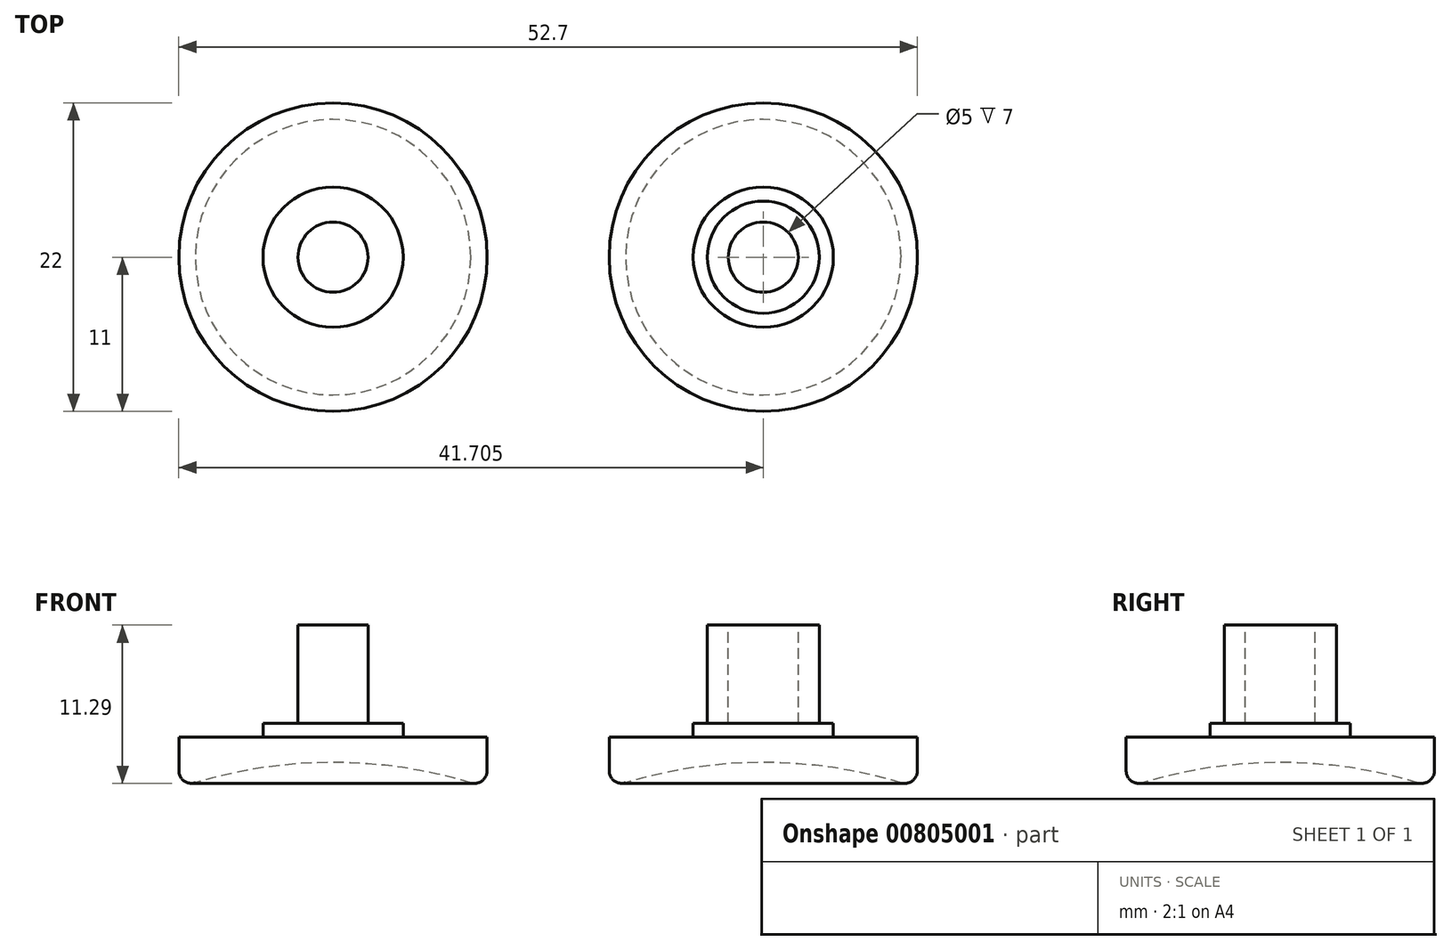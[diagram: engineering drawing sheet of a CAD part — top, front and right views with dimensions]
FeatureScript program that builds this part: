
annotation { "Feature Type Name" : "Feature", "Feature Type Description" : "" }
export const myFeature = defineFeature(function(context is Context, id is Id, definition is map)
    precondition{}
    {
        {
            var Q0;
            Q0=qCreatedBy(makeId("Top.planeOp"),FACE);
            var sketch = newSketch(context, id + "F0", { "sketchPlane" : qUnion([Q0])});
            skCircle(sketch, "E0", {"center": v(59.41, 64.06) * mm, "radius": 11 * mm});
            skSolve(sketch);
        }
        {
            var Q0;
            Q0=makeQuery(id+"F0.imprint","IMPRINT",FACE,{"disambiguationData":[TD([[makeQuery(id+"F0.imprint","IMPRINT",EDGE,{"derivedFrom":sQuery(id+"F0.wireOp",EDGE,"E0")}),1.0]])]});
            var Q1;
            Q1=makeQuery(id+"F0.imprint","IMPRINT",FACE,{"disambiguationData":[TD([[makeQuery(id+"F0.imprint","IMPRINT",EDGE,{"derivedFrom":sQuery(id+"F0.wireOp",EDGE,"2bYrixF8-2V4G-PsJT-iCTY-IxQZrD0WGVvQ")}),1.0]])]});
            extrude(context, id + "F1", {"entities" : qUnion([Q0, Q1]), "depth" : 3.5 * mm, "offsetDistance" : 25 * mm});
        }
        {
            var Q0;
            Q0=makeQuery(id+"F1.opExtrude","CAP_FACE",FACE,{"disambiguationData":[OSD([sQuery(id+"F0.wireOp",EDGE,"E0")])],"isStart":false});
            var sketch = newSketch(context, id + "F2", { "sketchPlane" : qUnion([Q0])});
            skPoint(sketch, "E1", {"position": v(59.41, 64.06) * mm});
            skCircle(sketch, "E2", {"center": v(59.41, 64.06) * mm, "radius": 5 * mm});
            skSolve(sketch);
        }
        {
            var Q0;
            Q0=qSketchRegion(id+"F2",true);
            extrude(context, id + "F3", {"entities" : qUnion([Q0]), "operationType" : NewBodyOperationType.ADD, "depth" : 1 * mm, "offsetDistance" : 25 * mm});
        }
        {
            var Q0;
            Q0=makeQuery(id+"F3.opExtrude","CAP_FACE",FACE,{"disambiguationData":[OSD([sQuery(id+"F2.wireOp",EDGE,"E2")])],"isStart":false});
            var sketch = newSketch(context, id + "F4", { "sketchPlane" : qUnion([Q0])});
            skPoint(sketch, "E3", {"position": v(59.41, 64.06) * mm});
            skCircle(sketch, "E4", {"center": v(59.41, 64.06) * mm, "radius": 4 * mm});
            skSolve(sketch);
        }
        {
            var Q0;
            Q0=makeQuery(id+"F4.imprint","IMPRINT",FACE,{"disambiguationData":[TD([[makeQuery(id+"F4.imprint","IMPRINT",EDGE,{"derivedFrom":sQuery(id+"F4.wireOp",EDGE,"E4")}),1.0]])]});
            extrude(context, id + "F5", {"entities" : qUnion([Q0]), "operationType" : NewBodyOperationType.ADD, "depth" : 7 * mm, "offsetDistance" : 25 * mm});
        }
        {
            var Q0;
            Q0=makeQuery(id+"F1.opExtrude","CAP_FACE",FACE,{"disambiguationData":[OSD([sQuery(id+"F0.wireOp",EDGE,"E0")])],"isStart":true});
            var sketch = newSketch(context, id + "F6", { "sketchPlane" : qUnion([Q0])});
            skCircle(sketch, "E5", {"center": v(59.41, -64.06) * mm, "radius": 1.35 * mm});
            skSolve(sketch);
        }
        {
            var Q0;
            Q0=makeQuery(id+"F6.imprint","IMPRINT",FACE,{"disambiguationData":[TD([[makeQuery(id+"F6.imprint","IMPRINT",EDGE,{"derivedFrom":sQuery(id+"F6.wireOp",EDGE,"E5")}),1.0]])]});
            extrude(context, id + "F7", {"entities" : qUnion([Q0]), "operationType" : NewBodyOperationType.ADD, "depth" : 32.3 * mm, "offsetDistance" : 25 * mm});
        }
        {
            var Q0;
            Q0=makeQuery(id+"F7.opExtrude","CAP_FACE",FACE,{"disambiguationData":[OSD([sQuery(id+"F6.wireOp",EDGE,"E5")])],"isStart":false});
            var sketch = newSketch(context, id + "F8", { "sketchPlane" : qUnion([Q0])});
            skCircle(sketch, "E6", {"center": v(59.41, -64.06) * mm, "radius": 34 * mm});
            skLineSegment(sketch, "E7", {"start": v(59.41, -64.06) * mm, "end": v(93.41, -64.06) * mm});
            skLineSegment(sketch, "E8", {"start": v(59.41, -64.06) * mm, "end": v(25.41, -64.06) * mm});
            skSolve(sketch);
        }
        {
            var Q0;
            {var subQ0=sQuery(id+"F8.wireOp",EDGE,"E7");var subQ1=sQuery(id+"F8.wireOp",EDGE,"E6");var subQ2=makeQuery(id+"F8.imprint","INTERSECT",VERTEX,{"derivedFrom":[subQ1,subQ0]});Q0=makeQuery(id+"F8.imprint","IMPRINT",FACE,{"disambiguationData":[TD([[makeQuery(id+"F8.imprint","IMPRINT",EDGE,{"disambiguationData":[TD([[subQ2,-1.0]])],"derivedFrom":subQ1}),1.0]])]});}
            var Q1;
            {var subQ0=sQuery(id+"F8.wireOp",EDGE,"E8");var subQ1=sQuery(id+"F8.wireOp",EDGE,"E7");var subQ2=makeQuery(id+"F8.imprint","INTERSECT",VERTEX,{"derivedFrom":[subQ1,subQ0]});Q1=makeQuery(id+"F8.imprint","IMPRINT",FACE,{"disambiguationData":[TD([[makeQuery(id+"F8.imprint","IMPRINT",EDGE,{"disambiguationData":[TD([[subQ2,-1.0]])],"derivedFrom":subQ1}),1.0]])]});}
            var Q2;
            Q2=sQuery(id+"F8.wireOp",EDGE,"E7");
            revolve(context, id + "F9", {"operationType" : NewBodyOperationType.REMOVE, "surfaceOperationType" : NewSurfaceOperationType.NEW, "entities" : qUnion([Q0, Q1]), "axis" : qUnion([Q2]), "revolveType" : RevolveType.FULL});
        }
        {
            var Q0;
            Q0=makeQuery(id+"F9.boolean.opBoolean","INTERSECT",EDGE,{"derivedFrom":[makeQuery(id+"F1.opExtrude","CAP_FACE",FACE,{"disambiguationData":[OSD([sQuery(id+"F0.wireOp",EDGE,"E0")])],"isStart":true}),makeQuery(id+"F9.opRevolve","SWEPT_FACE",FACE,{"disambiguationData":[OSD([sQuery(id+"F8.wireOp",EDGE,"E6")])]})]});
            fillet(context, id + "F10", {"entities" : qUnion([Q0]), "radius" : 5 * mm, "tangentPropagation" : true, "allowEdgeOverflow" : false});
        }
        {
            var Q0;
            {var subQ0=sQuery(id+"F0.wireOp",EDGE,"E0");Q0=makeQuery(id+"F10.opFillet","BLEND_EDGE",EDGE,{"blendedFrom":[makeQuery(id+"F9.boolean.opBoolean","INTERSECT",EDGE,{"derivedFrom":[makeQuery(id+"F1.opExtrude","CAP_FACE",FACE,{"disambiguationData":[OSD([subQ0])],"isStart":true}),makeQuery(id+"F9.opRevolve","SWEPT_FACE",FACE,{"disambiguationData":[OSD([sQuery(id+"F8.wireOp",EDGE,"E6")])]})]}),makeQuery(id+"F1.opExtrude","SWEPT_FACE",FACE,{"disambiguationData":[OSD([subQ0])]})],"blendedInto":[makeQuery(id+"F1.opExtrude","SWEPT_FACE",FACE,{"disambiguationData":[OSD([subQ0])]})]});}
            fillet(context, id + "F11", {"entities" : qUnion([Q0]), "radius" : 0.9 * mm, "tangentPropagation" : true, "allowEdgeOverflow" : false});
        }
        {
            var Q0;
            Q0=makeQuery(id+"F1.opExtrude","SWEPT_BODY",BODY,{"disambiguationData":[OSD([sQuery(id+"F0.wireOp",EDGE,"E0")])]});
            transform(context, id + "F12", {"entities" : qUnion([Q0]), "transformType" : TransformType.TRANSLATION_3D, "dx" : -30.7 * mm, "dy" : 0 * mm, "dz" : 0 * mm, "makeCopy" : true});
        }
        {
            var Q0;
            Q0=makeQuery(id+"F5.opExtrude","CAP_FACE",FACE,{"disambiguationData":[OSD([sQuery(id+"F4.wireOp",EDGE,"E4")])],"isStart":false});
            var sketch = newSketch(context, id + "F13", { "sketchPlane" : qUnion([Q0])});
            skCircle(sketch, "E9", {"center": v(59.41, 64.06) * mm, "radius": 2.5 * mm});
            skSolve(sketch);
        }
        {
            var Q0;
            Q0=makeQuery(id+"F13.imprint","IMPRINT",FACE,{"disambiguationData":[TD([[makeQuery(id+"F13.imprint","IMPRINT",EDGE,{"derivedFrom":sQuery(id+"F13.wireOp",EDGE,"E9")}),1.0]])]});
            extrude(context, id + "F14", {"entities" : qUnion([Q0]), "operationType" : NewBodyOperationType.REMOVE, "oppositeDirection" : true, "depth" : 7 * mm, "offsetDistance" : 25 * mm});
        }
        {
            var Q0;
            Q0=makeQuery(id+"F12.opPattern","COPY",FACE,{"derivedFrom":makeQuery(id+"F5.opExtrude","CAP_FACE",FACE,{"disambiguationData":[OSD([sQuery(id+"F4.wireOp",EDGE,"E4")])],"isStart":false}),"instanceName":"1"});
            var sketch = newSketch(context, id + "F15", { "sketchPlane" : qUnion([Q0])});
            skCircle(sketch, "E10", {"center": v(28.71, 64.06) * mm, "radius": 2.5 * mm});
            skSolve(sketch);
        }
        {
            var Q0;
            Q0=makeQuery(id+"F15.imprint","IMPRINT",FACE,{"disambiguationData":[TD([[makeQuery(id+"F15.imprint","IMPRINT",EDGE,{"derivedFrom":sQuery(id+"F15.wireOp",EDGE,"E10")}),-1.0]])]});
            extrude(context, id + "F16", {"entities" : qUnion([Q0]), "operationType" : NewBodyOperationType.REMOVE, "oppositeDirection" : true, "depth" : 7 * mm, "offsetDistance" : 25 * mm});
        }
    });
